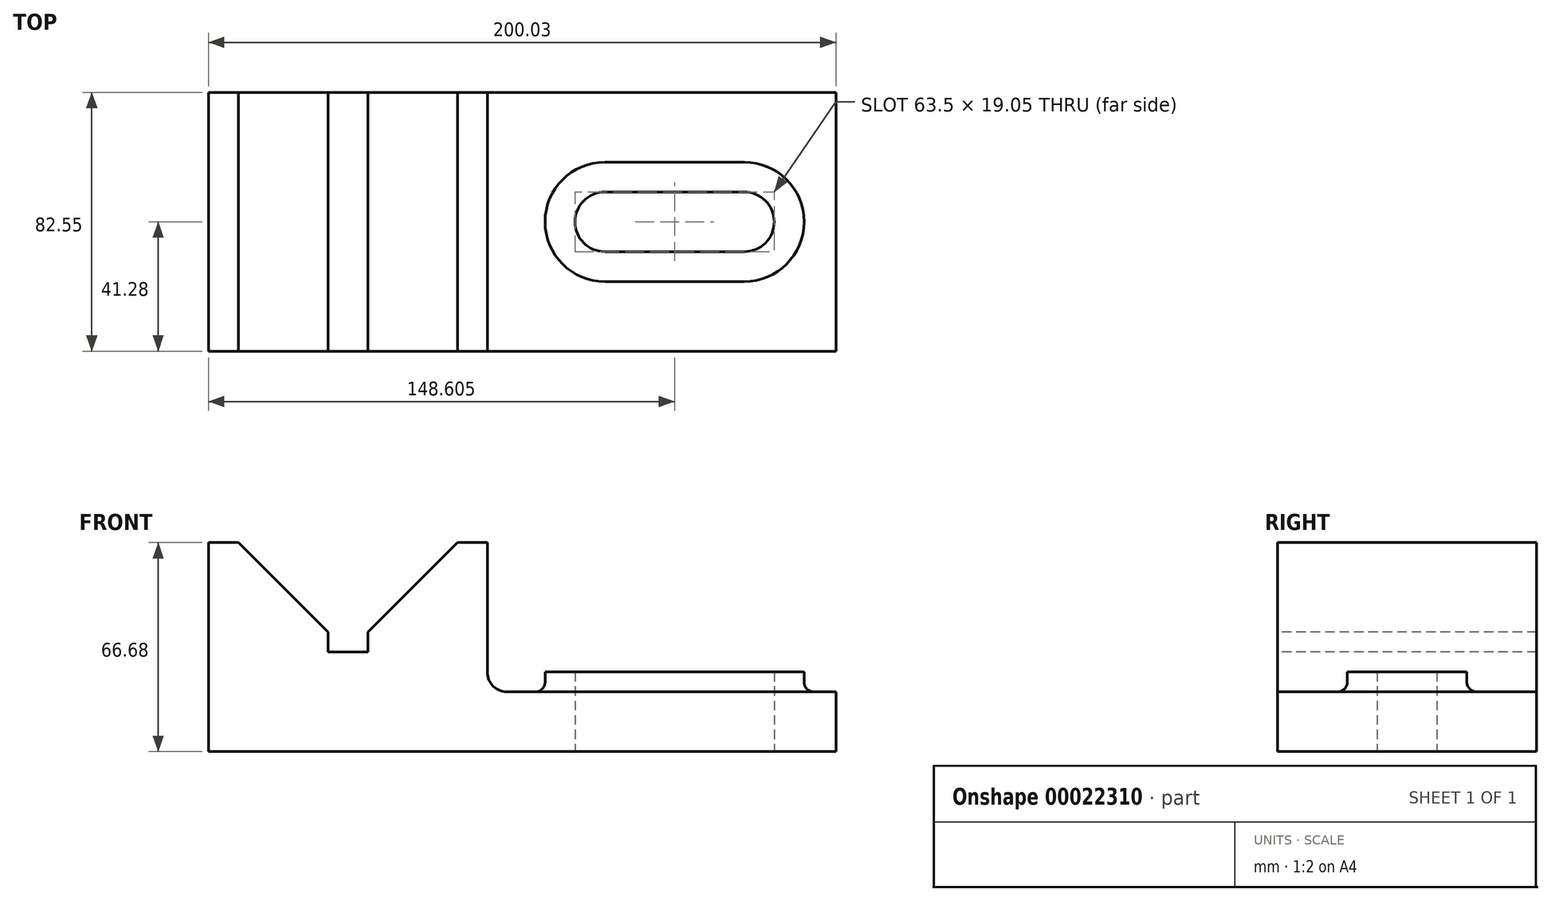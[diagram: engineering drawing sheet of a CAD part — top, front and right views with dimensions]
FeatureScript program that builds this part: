
annotation { "Feature Type Name" : "Feature", "Feature Type Description" : "" }
export const myFeature = defineFeature(function(context is Context, id is Id, definition is map)
    precondition{}
    {
        {
            var Q0;
            Q0=qCreatedBy(makeId("Top.planeOp"),FACE);
            var sketch = newSketch(context, id + "F0", { "sketchPlane" : qUnion([Q0])});
            skLineSegment(sketch, "E0.bottom", {"start": v(-97.5, -5.99) * mm, "end": v(102.53, -5.99) * mm});
            skLineSegment(sketch, "E0.top", {"start": v(-97.5, -88.54) * mm, "end": v(102.53, -88.54) * mm});
            skLineSegment(sketch, "E0.left", {"start": v(-97.5, -5.99) * mm, "end": v(-97.5, -88.54) * mm});
            skLineSegment(sketch, "E0.right", {"start": v(102.53, -5.99) * mm, "end": v(102.53, -88.54) * mm});
            skSolve(sketch);
        }
        {
            var Q0;
            Q0=makeQuery(id+"F0.imprint","IMPRINT",FACE,{"disambiguationData":[TD([[makeQuery(id+"F0.imprint","IMPRINT",EDGE,{"derivedFrom":sQuery(id+"F0.wireOp",EDGE,"E0.bottom")}),-1.0]])]});
            extrude(context, id + "F1", {"entities" : qUnion([Q0]), "depth" : 66.67 * mm});
        }
        {
            var Q0;
            Q0=makeQuery(id+"F1.opExtrude","SWEPT_FACE",FACE,{"disambiguationData":[OSD([sQuery(id+"F0.wireOp",EDGE,"E0.top")])]});
            var sketch = newSketch(context, id + "F2", { "sketchPlane" : qUnion([Q0])});
            skLineSegment(sketch, "E1", {"start": v(-87.97, 66.68) * mm, "end": v(-59.4, 38.1) * mm});
            skLineSegment(sketch, "E2", {"start": v(-59.4, 38.1) * mm, "end": v(-59.4, 31.75) * mm});
            skLineSegment(sketch, "E3", {"start": v(-46.7, 31.75) * mm, "end": v(-46.7, 38.1) * mm});
            skLineSegment(sketch, "E4", {"start": v(-46.7, 38.1) * mm, "end": v(-18.12, 66.68) * mm});
            skLineSegment(sketch, "E5", {"start": v(-59.4, 31.75) * mm, "end": v(-46.7, 31.75) * mm});
            skLineSegment(sketch, "E6", {"start": v(-59.4, 38.1) * mm, "end": v(102.53, 38.1) * mm});
            skLineSegment(sketch, "E7", {"start": v(102.53, 38.1) * mm, "end": v(-97.5, 38.1) * mm});
            skLineSegment(sketch, "E8.bottom", {"start": v(-97.5, 66.68) * mm, "end": v(-8.6, 66.68) * mm});
            skLineSegment(sketch, "E8.top", {"start": v(-97.5, 0) * mm, "end": v(-8.6, 0) * mm});
            skLineSegment(sketch, "E8.left", {"start": v(-97.5, 66.68) * mm, "end": v(-97.5, 0) * mm});
            skLineSegment(sketch, "E8.right", {"start": v(-8.6, 66.68) * mm, "end": v(-8.6, 0) * mm});
            skSolve(sketch);
        }
        {
            var Q0;
            {var subQ2=sQuery(id+"F2.wireOp",EDGE,"E1");Q0=makeQuery(id+"F2.imprint","IMPRINT",FACE,{"disambiguationData":[TD([[makeQuery(id+"F2.imprint","IMPRINT",EDGE,{"derivedFrom":subQ2}),1.0]])]});}
            var Q1;
            {var subQ2=sQuery(id+"F2.wireOp",EDGE,"E2");Q1=makeQuery(id+"F2.imprint","IMPRINT",FACE,{"disambiguationData":[TD([[makeQuery(id+"F2.imprint","IMPRINT",EDGE,{"derivedFrom":subQ2}),1.0]])]});}
            extrude(context, id + "F3", {"entities" : qUnion([Q0, Q1]), "operationType" : NewBodyOperationType.REMOVE, "oppositeDirection" : true, "depth" : 82.55 * mm});
        }
        {
            var Q0;
            Q0=makeQuery(id+"F1.opExtrude","SWEPT_FACE",FACE,{"disambiguationData":[OSD([sQuery(id+"F0.wireOp",EDGE,"E0.top")])]});
            var sketch = newSketch(context, id + "F4", { "sketchPlane" : qUnion([Q0])});
            skLineSegment(sketch, "E9.bottom", {"start": v(-8.6, 66.68) * mm, "end": v(102.53, 66.68) * mm});
            skLineSegment(sketch, "E9.top", {"start": v(-2.25, 19.05) * mm, "end": v(102.53, 19.05) * mm});
            skLineSegment(sketch, "E9.left", {"start": v(-8.6, 66.68) * mm, "end": v(-8.6, 25.4) * mm});
            skLineSegment(sketch, "E9.right", {"start": v(102.53, 66.68) * mm, "end": v(102.53, 19.05) * mm});
            skPoint(sketch, "E10.visualSharp", {"position": v(-8.6, 19.05) * mm});
            skArc(sketch, "E10.filletArc", {"start": v(-8.6, 25.4) * mm, "mid": v(-6.74, 20.9) * mm, "end": v(-2.25, 19.05) * mm});
            skSolve(sketch);
        }
        {
            var Q0;
            Q0=makeQuery(id+"F4.imprint","IMPRINT",FACE,{"disambiguationData":[TD([[makeQuery(id+"F4.imprint","IMPRINT",EDGE,{"derivedFrom":sQuery(id+"F4.wireOp",EDGE,"E9.bottom")}),-1.0]])]});
            extrude(context, id + "F5", {"entities" : qUnion([Q0]), "operationType" : NewBodyOperationType.REMOVE, "oppositeDirection" : true, "depth" : 95.25 * mm});
        }
        {
            var Q0;
            Q0=makeQuery(id+"F5.boolean.opBoolean","COPY",FACE,{"derivedFrom":makeQuery(id+"F5.opExtrude","SWEPT_FACE",FACE,{"disambiguationData":[OSD([sQuery(id+"F4.wireOp",EDGE,"E9.top")])]})});
            var sketch = newSketch(context, id + "F6", { "sketchPlane" : qUnion([Q0])});
            skLineSegment(sketch, "E11.bottom", {"start": v(28.88, -56.79) * mm, "end": v(73.33, -56.79) * mm});
            skLineSegment(sketch, "E11.top", {"start": v(28.88, -37.74) * mm, "end": v(73.33, -37.74) * mm});
            skLineSegment(sketch, "E11.left", {"start": v(28.88, -56.79) * mm, "end": v(28.88, -37.74) * mm});
            skLineSegment(sketch, "E11.right", {"start": v(73.33, -56.79) * mm, "end": v(73.33, -37.74) * mm});
            skArc(sketch, "E12", {"start": v(73.33, -56.79) * mm, "mid": v(82.86, -47.26) * mm, "end": v(73.33, -37.74) * mm});
            skArc(sketch, "E13", {"start": v(28.88, -37.74) * mm, "mid": v(19.36, -47.26) * mm, "end": v(28.88, -56.79) * mm});
            skLineSegment(sketch, "E14.bottom", {"start": v(28.88, -66.31) * mm, "end": v(73.33, -66.31) * mm});
            skLineSegment(sketch, "E14.top", {"start": v(28.88, -28.21) * mm, "end": v(73.33, -28.21) * mm});
            skLineSegment(sketch, "E14.left", {"start": v(28.88, -66.31) * mm, "end": v(28.88, -28.21) * mm});
            skLineSegment(sketch, "E14.right", {"start": v(73.33, -66.31) * mm, "end": v(73.33, -28.21) * mm});
            skArc(sketch, "E15", {"start": v(28.88, -28.21) * mm, "mid": v(9.83, -47.26) * mm, "end": v(28.88, -66.31) * mm});
            skArc(sketch, "E16", {"start": v(73.33, -66.31) * mm, "mid": v(92.38, -47.26) * mm, "end": v(73.33, -28.21) * mm});
            skSolve(sketch);
        }
        {
            var Q0;
            {var subQ2=sQuery(id+"F6.wireOp",EDGE,"E13");Q0=makeQuery(id+"F6.imprint","IMPRINT",FACE,{"disambiguationData":[TD([[makeQuery(id+"F6.imprint","IMPRINT",EDGE,{"derivedFrom":subQ2}),-1.0]])]});}
            var Q1;
            {var subQ2=sQuery(id+"F6.wireOp",EDGE,"E11.bottom");Q1=makeQuery(id+"F6.imprint","IMPRINT",FACE,{"disambiguationData":[TD([[makeQuery(id+"F6.imprint","IMPRINT",EDGE,{"derivedFrom":subQ2}),-1.0]])]});}
            var Q2;
            {var subQ2=sQuery(id+"F6.wireOp",EDGE,"E12");Q2=makeQuery(id+"F6.imprint","IMPRINT",FACE,{"disambiguationData":[TD([[makeQuery(id+"F6.imprint","IMPRINT",EDGE,{"derivedFrom":subQ2}),-1.0]])]});}
            var Q3;
            {var subQ2=sQuery(id+"F6.wireOp",EDGE,"E11.top");Q3=makeQuery(id+"F6.imprint","IMPRINT",FACE,{"disambiguationData":[TD([[makeQuery(id+"F6.imprint","IMPRINT",EDGE,{"derivedFrom":subQ2}),1.0]])]});}
            extrude(context, id + "F7", {"entities" : qUnion([Q0, Q1, Q2, Q3]), "operationType" : NewBodyOperationType.ADD, "depth" : 6.35 * mm});
        }
        {
            var Q0;
            Q0=makeQuery(id+"F7.opExtrude","CAP_EDGE",EDGE,{"disambiguationData":[OSD([sQuery(id+"F6.wireOp",EDGE,"E14.bottom")])],"isStart":true});
            fillet(context, id + "F8", {"entities" : qUnion([Q0]), "radius" : 3.17 * mm, "tangentPropagation" : true, "allowEdgeOverflow" : false});
        }
        {
            var Q0;
            Q0=makeQuery(id+"F7.boolean.opBoolean","SPLIT",FACE,{"disambiguationData":[TD([makeQuery(id+"F7.opExtrude","SWEPT_FACE",FACE,{"disambiguationData":[OSD([sQuery(id+"F6.wireOp",EDGE,"E11.bottom")])]})])],"derivedFrom":makeQuery(id+"F5.boolean.opBoolean","COPY",FACE,{"derivedFrom":makeQuery(id+"F5.opExtrude","SWEPT_FACE",FACE,{"disambiguationData":[OSD([sQuery(id+"F4.wireOp",EDGE,"E9.top")])]})})});
            extrude(context, id + "F9", {"entities" : qUnion([Q0]), "operationType" : NewBodyOperationType.REMOVE, "oppositeDirection" : true, "depth" : 127 * mm});
        }
    });
